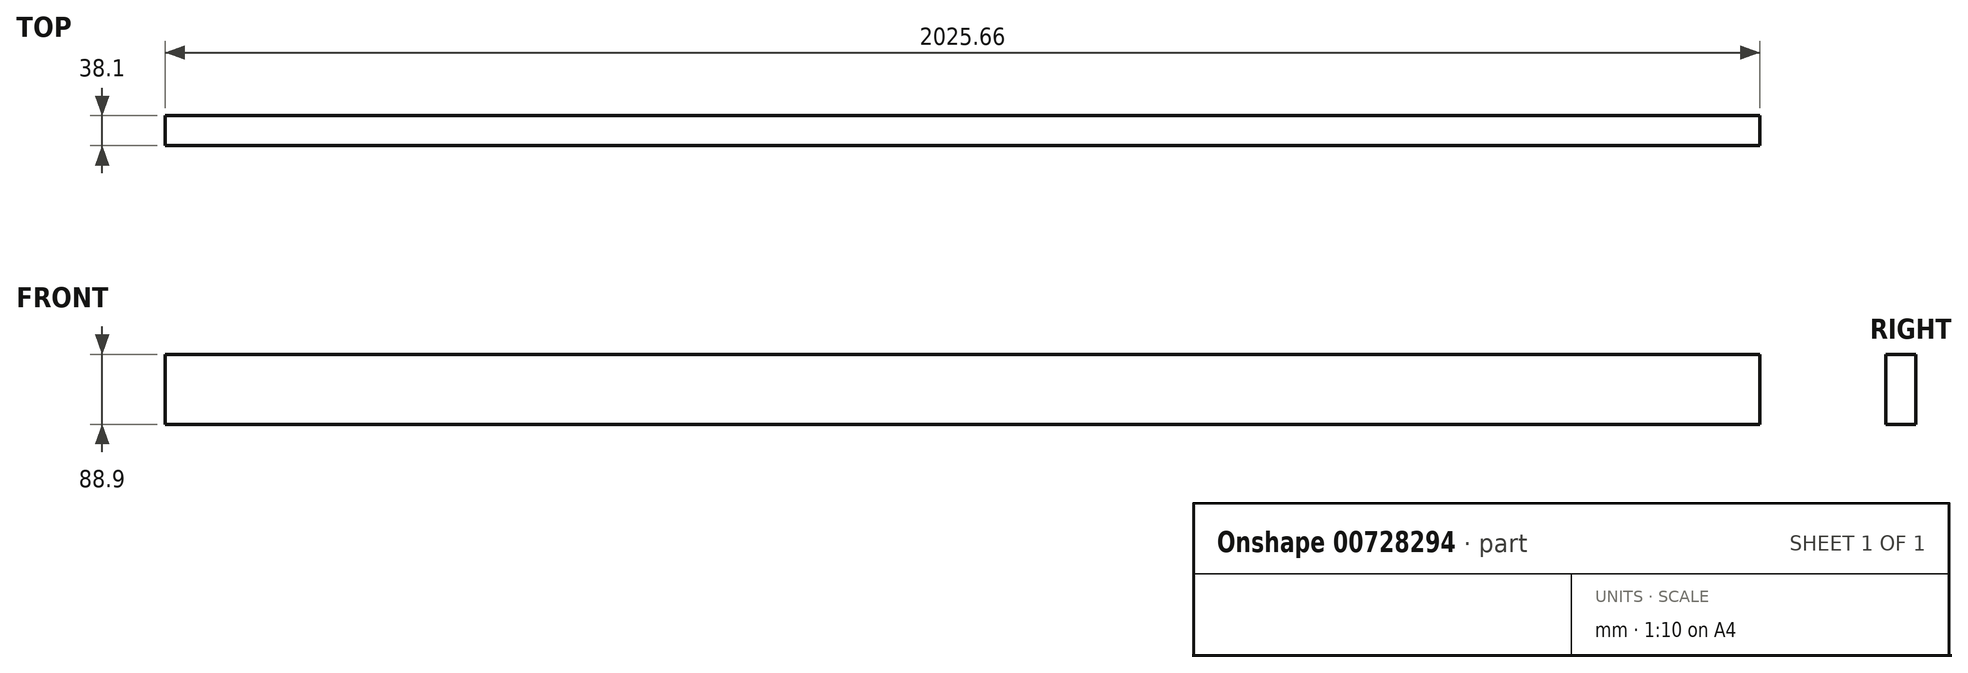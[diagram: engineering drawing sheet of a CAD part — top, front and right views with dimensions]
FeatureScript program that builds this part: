
annotation { "Feature Type Name" : "Feature", "Feature Type Description" : "" }
export const myFeature = defineFeature(function(context is Context, id is Id, definition is map)
    precondition{}
    {
        {
            var Q0;
            Q0=qCreatedBy(makeId("Front.planeOp"),FACE);
            var sketch = newSketch(context, id + "F0", { "sketchPlane" : qUnion([Q0])});
            skLineSegment(sketch, "E0.bottom", {"start": v(-1012.83, -44.45) * mm, "end": v(1012.83, -44.45) * mm});
            skLineSegment(sketch, "E0.top", {"start": v(-1012.83, 44.45) * mm, "end": v(1012.83, 44.45) * mm});
            skLineSegment(sketch, "E0.left", {"start": v(-1012.83, -44.45) * mm, "end": v(-1012.83, 44.45) * mm});
            skLineSegment(sketch, "E0.right", {"start": v(1012.83, -44.45) * mm, "end": v(1012.83, 44.45) * mm});
            skPoint(sketch, "E0.middle", {"position": v(0, 0) * mm});
            skSolve(sketch);
        }
        {
            var Q0;
            Q0=qSketchRegion(id+"F0",true);
            extrude(context, id + "F1", {"entities" : qUnion([Q0]), "depth" : 38.1 * mm, "offsetDistance" : 25.4 * mm});
        }
    });
